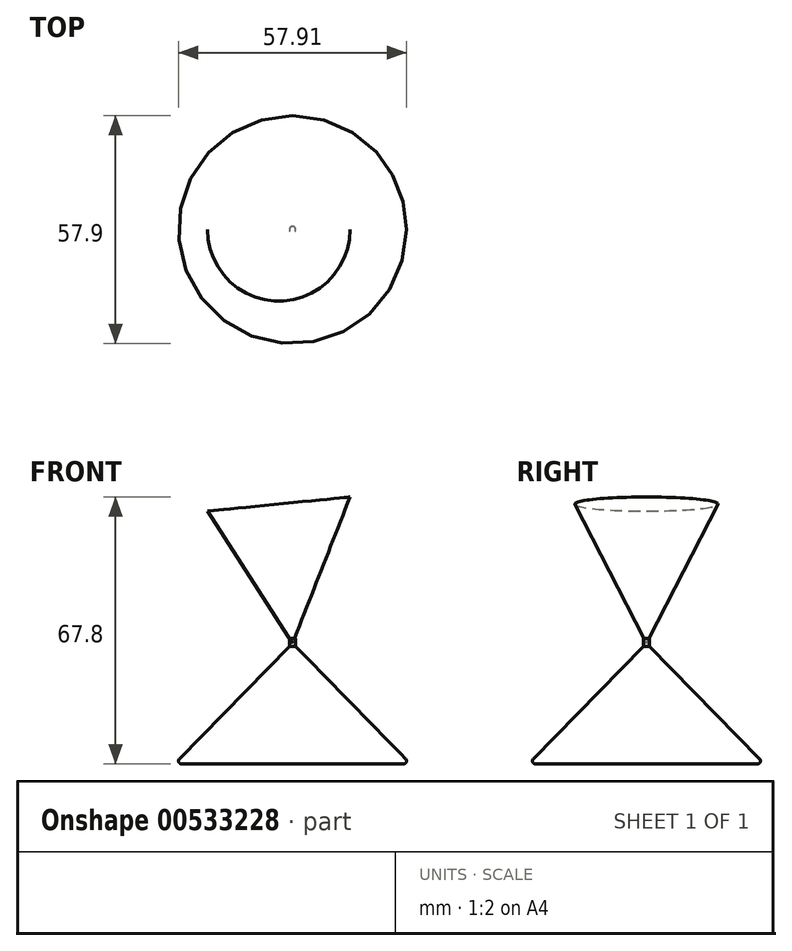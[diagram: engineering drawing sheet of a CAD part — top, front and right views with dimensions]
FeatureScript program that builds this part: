
annotation { "Feature Type Name" : "Feature", "Feature Type Description" : "" }
export const myFeature = defineFeature(function(context is Context, id is Id, definition is map)
    precondition{}
    {
        {
            var Q0;
            Q0=qCreatedBy(makeId("Front.planeOp"),FACE);
            var sketch = newSketch(context, id + "F0", { "sketchPlane" : qUnion([Q0])});
            skLineSegment(sketch, "E0", {"start": v(-1.1, 0) * mm, "end": v(-1.1, -30.65) * mm});
            skLineSegment(sketch, "E1", {"start": v(-1.1, -30.65) * mm, "end": v(-31.1, -30.65) * mm});
            skLineSegment(sketch, "E2", {"start": v(-31.1, -30.65) * mm, "end": v(-1.1, 0) * mm});
            skLineSegment(sketch, "E3", {"start": v(-1.1, 0) * mm, "end": v(-4.6, 35.37) * mm});
            skLineSegment(sketch, "E4", {"start": v(-4.6, 35.37) * mm, "end": v(-22.7, 33.58) * mm});
            skLineSegment(sketch, "E5", {"start": v(-22.7, 33.58) * mm, "end": v(-1.1, 0) * mm});
            skLineSegment(sketch, "E6", {"start": v(-1.91, -0.82) * mm, "end": v(-1.91, 2.5) * mm});
            skSolve(sketch);
        }
        {
            var Q0;
            {var subQ0=sQuery(id+"F0.wireOp",EDGE,"E3");Q0=makeQuery(id+"F0.imprint","IMPRINT",FACE,{"disambiguationData":[TD([[makeQuery(id+"F0.imprint","IMPRINT",EDGE,{"derivedFrom":subQ0}),1.0]])]});}
            var Q1;
            Q1=sQuery(id+"F0.wireOp",EDGE,"E3");
            revolve(context, id + "F1", {"entities" : qUnion([Q0]), "axis" : qUnion([Q1]), "revolveType" : RevolveType.FULL});
        }
        {
            var Q0;
            {var subQ0=sQuery(id+"F0.wireOp",EDGE,"E0");Q0=makeQuery(id+"F0.imprint","IMPRINT",FACE,{"disambiguationData":[TD([[makeQuery(id+"F0.imprint","IMPRINT",EDGE,{"derivedFrom":subQ0}),-1.0]])]});}
            var Q1;
            {var subQ3=sQuery(id+"F0.wireOp",EDGE,"E6");Q1=makeQuery(id+"F0.imprint","IMPRINT",FACE,{"disambiguationData":[TD([[makeQuery(id+"F0.imprint","IMPRINT",EDGE,{"derivedFrom":subQ3}),-1.0]])]});}
            var Q2;
            Q2=sQuery(id+"F0.wireOp",EDGE,"E0");
            revolve(context, id + "F2", {"operationType" : NewBodyOperationType.ADD, "entities" : qUnion([Q0, Q1]), "axis" : qUnion([Q2]), "revolveType" : RevolveType.FULL});
        }
        {
            var Q0;
            Q0=makeQuery(id+"F2.opRevolve","SWEPT_EDGE",EDGE,{"disambiguationData":[OSD([sQuery(id+"F0.wireOp",EDGE,"E1"),sQuery(id+"F0.wireOp",EDGE,"E2")])]});
            fillet(context, id + "F3", {"entities" : qUnion([Q0]), "radius" : 0.76 * mm, "tangentPropagation" : true, "allowEdgeOverflow" : false});
        }
    });
